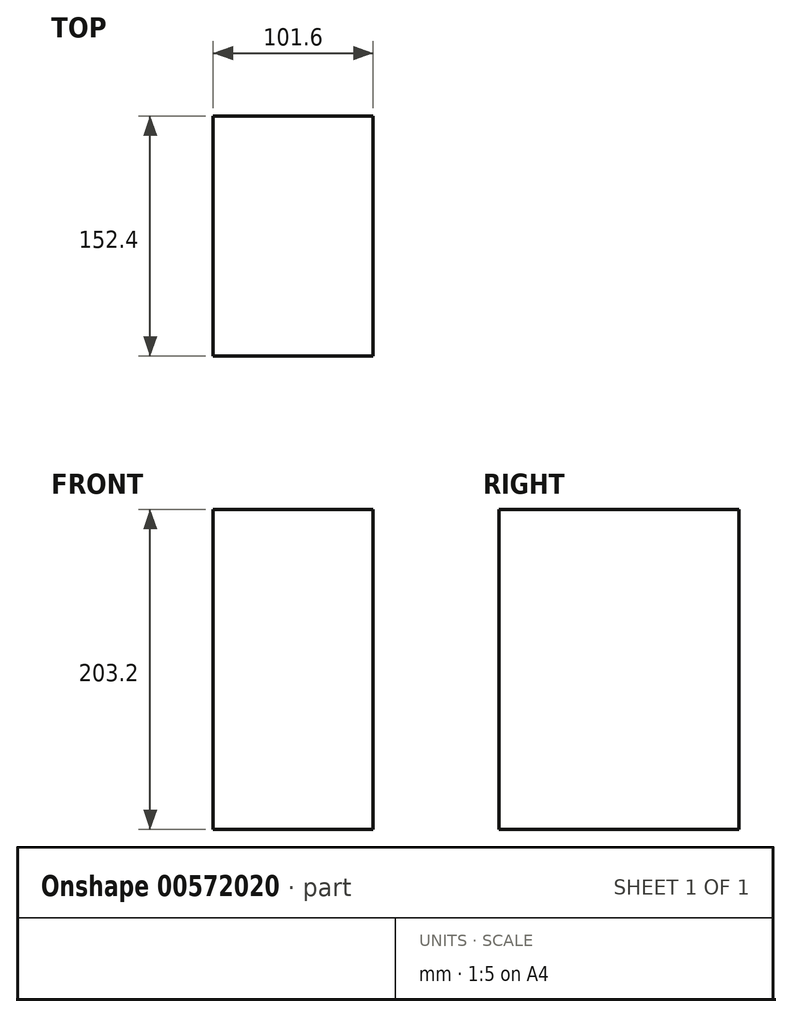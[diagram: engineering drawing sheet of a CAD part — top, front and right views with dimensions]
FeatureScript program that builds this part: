
annotation { "Feature Type Name" : "Feature", "Feature Type Description" : "" }
export const myFeature = defineFeature(function(context is Context, id is Id, definition is map)
    precondition{}
    {
        {
            var Q0;
            Q0=qCreatedBy(makeId("Top.planeOp"),FACE);
            var sketch = newSketch(context, id + "F0", { "sketchPlane" : qUnion([Q0])});
            skLineSegment(sketch, "E0.bottom", {"start": v(63.5, 0) * mm, "end": v(-38.1, 0) * mm});
            skLineSegment(sketch, "E0.top", {"start": v(63.5, 152.4) * mm, "end": v(-38.1, 152.4) * mm});
            skLineSegment(sketch, "E0.left", {"start": v(63.5, 0) * mm, "end": v(63.5, 152.4) * mm});
            skLineSegment(sketch, "E0.right", {"start": v(-38.1, 0) * mm, "end": v(-38.1, 152.4) * mm});
            skSolve(sketch);
        }
        {
            var Q0;
            Q0=makeQuery(id+"F0.imprint","IMPRINT",FACE,{"disambiguationData":[TD([[makeQuery(id+"F0.imprint","IMPRINT",EDGE,{"derivedFrom":sQuery(id+"F0.wireOp",EDGE,"E0.bottom")}),-1.0]])]});
            extrude(context, id + "F1", {"entities" : qUnion([Q0]), "depth" : 203.2 * mm, "offsetDistance" : 25.4 * mm});
        }
    });
